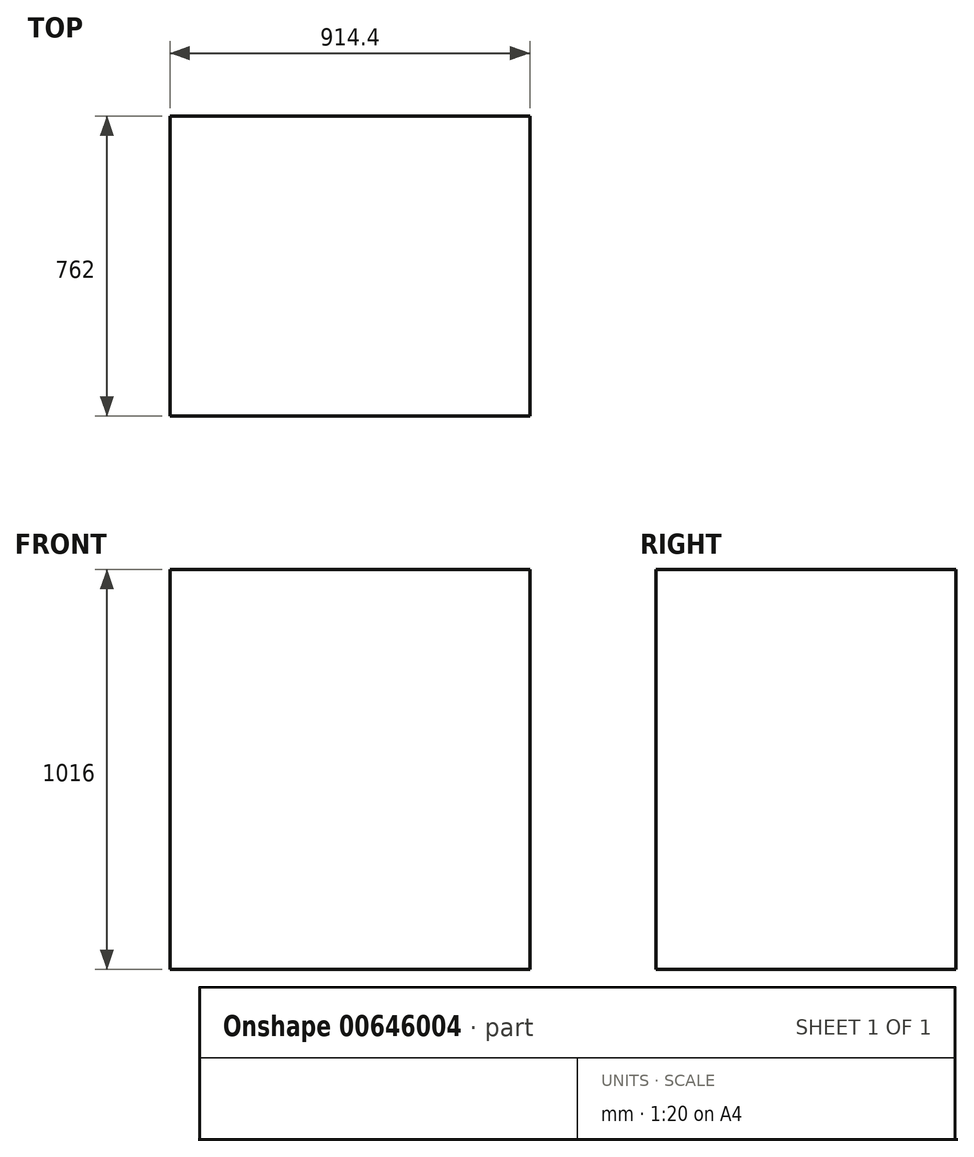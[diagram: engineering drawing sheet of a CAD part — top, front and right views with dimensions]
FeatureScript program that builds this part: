
annotation { "Feature Type Name" : "Feature", "Feature Type Description" : "" }
export const myFeature = defineFeature(function(context is Context, id is Id, definition is map)
    precondition{}
    {
        {
            var Q0;
            Q0=qCreatedBy(makeId("Top.planeOp"),FACE);
            var sketch = newSketch(context, id + "F0", { "sketchPlane" : qUnion([Q0])});
            skLineSegment(sketch, "E0.bottom", {"start": v(457.2, 381) * mm, "end": v(-457.2, 381) * mm});
            skLineSegment(sketch, "E0.top", {"start": v(457.2, -381) * mm, "end": v(-457.2, -381) * mm});
            skLineSegment(sketch, "E0.left", {"start": v(457.2, 381) * mm, "end": v(457.2, -381) * mm});
            skLineSegment(sketch, "E0.right", {"start": v(-457.2, 381) * mm, "end": v(-457.2, -381) * mm});
            skPoint(sketch, "E0.middle", {"position": v(0, 0) * mm});
            skSolve(sketch);
        }
        {
            var Q0;
            Q0=makeQuery(id+"F0.imprint","IMPRINT",FACE,{"disambiguationData":[TD([[makeQuery(id+"F0.imprint","IMPRINT",EDGE,{"derivedFrom":sQuery(id+"F0.wireOp",EDGE,"E0.bottom")}),1.0]])]});
            extrude(context, id + "F1", {"entities" : qUnion([Q0]), "depth" : 1016 * mm, "offsetDistance" : 25.4 * mm});
        }
    });
